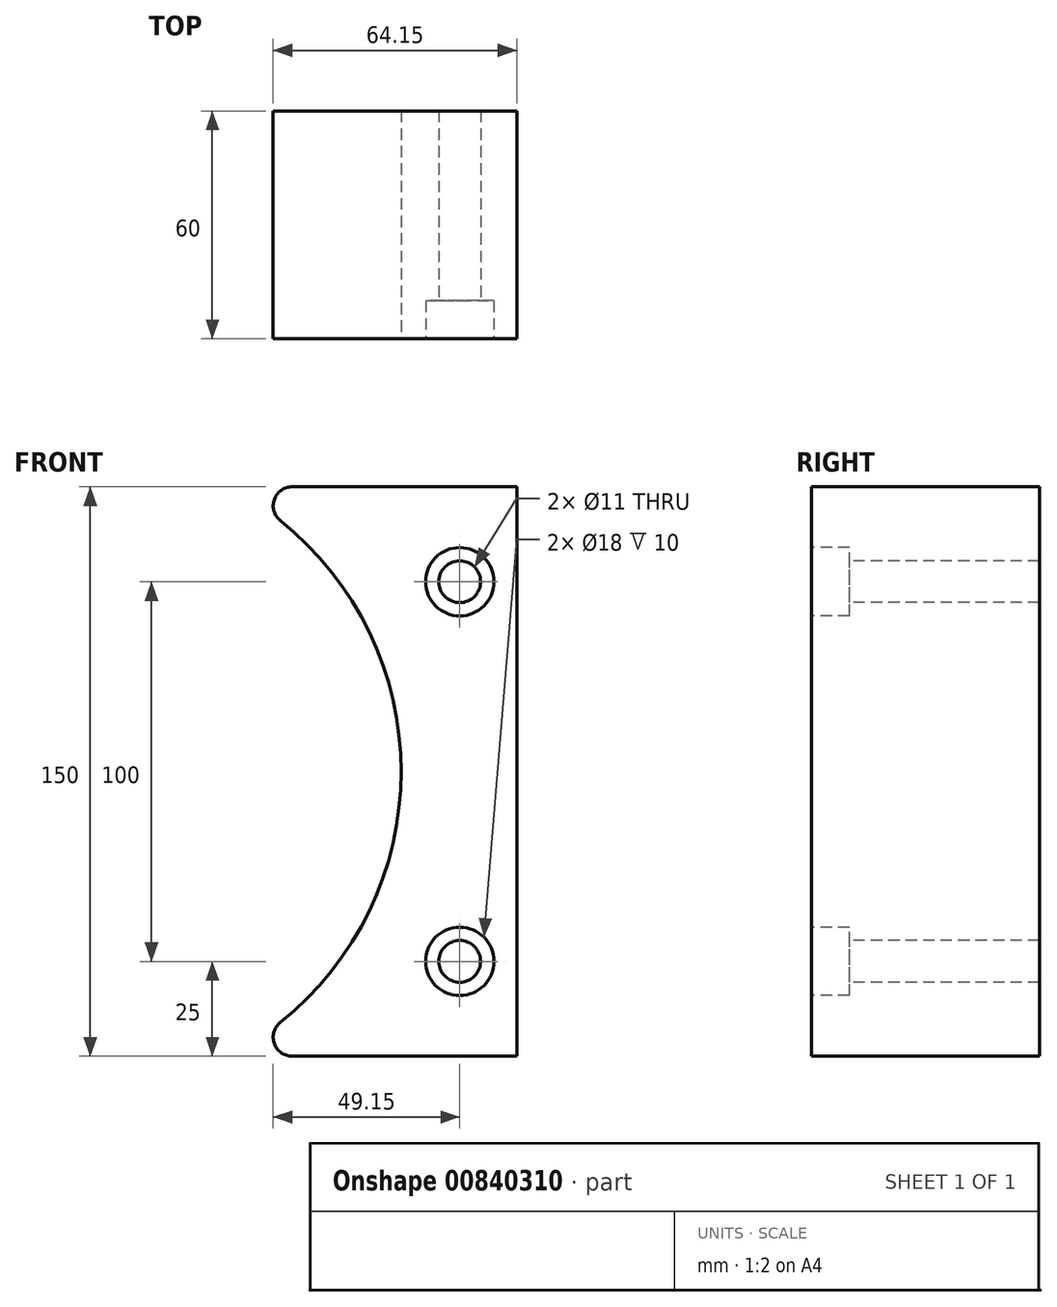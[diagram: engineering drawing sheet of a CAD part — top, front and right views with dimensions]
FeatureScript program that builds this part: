
annotation { "Feature Type Name" : "Feature", "Feature Type Description" : "" }
export const myFeature = defineFeature(function(context is Context, id is Id, definition is map)
    precondition{}
    {
        {
            var Q0;
            Q0=qCreatedBy(makeId("Front.planeOp"),FACE);
            var sketch = newSketch(context, id + "F0", { "sketchPlane" : qUnion([Q0])});
            skLineSegment(sketch, "E0.bottom", {"start": v(-37.5, 75) * mm, "end": v(37.5, 75) * mm});
            skLineSegment(sketch, "E0.top", {"start": v(-37.5, -75) * mm, "end": v(37.5, -75) * mm});
            skLineSegment(sketch, "E0.left", {"start": v(-37.5, 75) * mm, "end": v(-37.5, -75) * mm});
            skLineSegment(sketch, "E0.right", {"start": v(37.5, 75) * mm, "end": v(37.5, -75) * mm});
            skPoint(sketch, "E0.middle", {"position": v(0, 0) * mm});
            skSolve(sketch);
        }
        {
            var Q0;
            Q0 = qSketchRegion(id + "F0", true);
            extrude(context, id + "F1", {"entities" : qUnion([Q0]), "endBound" : BoundingType.SYMMETRIC, "depth" : 60 * mm, "offsetDistance" : 25 * mm});
        }
        {
            var Q0;
            Q0=makeQuery(id+"F1.opExtrude","CAP_FACE",FACE,{"disambiguationData":[OSD([sQuery(id+"F0.wireOp",EDGE,"E0.bottom"),sQuery(id+"F0.wireOp",EDGE,"E0.top"),sQuery(id+"F0.wireOp",EDGE,"E0.left"),sQuery(id+"F0.wireOp",EDGE,"E0.right")])],"isStart":false});
            var sketch = newSketch(context, id + "F2", { "sketchPlane" : qUnion([Q0])});
            skCircle(sketch, "E1", {"center": v(-77.5, 0) * mm, "radius": 84.55 * mm});
            skArc(sketch, "E2", {"start": v(-21.65, 75) * mm, "mid": v(-26.37, 71.65) * mm, "end": v(-24.77, 66.1) * mm});
            skArc(sketch, "E3", {"start": v(-24.77, -66.1) * mm, "mid": v(-26.37, -71.65) * mm, "end": v(-21.65, -75) * mm});
            skSolve(sketch);
        }
        {
            var Q0;
            Q0 = qSketchRegion(id + "F2", true);
            var Q1;
            {var subQ0=sQuery(id+"F2.wireOp",EDGE,"E2");Q1=makeQuery(id+"F2.imprint","IMPRINT",FACE,{"disambiguationData":[TD([[makeQuery(id+"F2.imprint","IMPRINT",EDGE,{"derivedFrom":subQ0}),-1.0]])]});}
            var Q2;
            {var subQ0=sQuery(id+"F2.wireOp",EDGE,"E3");Q2=makeQuery(id+"F2.imprint","IMPRINT",FACE,{"disambiguationData":[TD([[makeQuery(id+"F2.imprint","IMPRINT",EDGE,{"derivedFrom":subQ0}),-1.0]])]});}
            extrude(context, id + "F3", {"entities" : qUnion([Q0, Q1, Q2]), "operationType" : NewBodyOperationType.REMOVE, "endBound" : BoundingType.THROUGH_ALL, "oppositeDirection" : true, "depth" : 25 * mm, "offsetDistance" : 25 * mm});
        }
        {
            var Q0;
            Q0=makeQuery(id+"F1.opExtrude","CAP_FACE",FACE,{"disambiguationData":[OSD([sQuery(id+"F0.wireOp",EDGE,"E0.bottom"),sQuery(id+"F0.wireOp",EDGE,"E0.top"),sQuery(id+"F0.wireOp",EDGE,"E0.left"),sQuery(id+"F0.wireOp",EDGE,"E0.right")])],"isStart":false});
            var sketch = newSketch(context, id + "F4", { "sketchPlane" : qUnion([Q0])});
            skPoint(sketch, "E4", {"position": v(22.5, 50) * mm});
            skPoint(sketch, "E5", {"position": v(22.5, -50) * mm});
            skSolve(sketch);
        }
        {
            var Q0;
            Q0=sQuery(id+"F4.wireOp",VERTEX,"E4");
            var Q1;
            Q1=sQuery(id+"F4.wireOp",VERTEX,"E5");
            var Q2;
            Q2=makeQuery(id+"F1.opExtrude","SWEPT_BODY",BODY,{"disambiguationData":[OSD([sQuery(id+"F0.wireOp",EDGE,"E0.bottom"),sQuery(id+"F0.wireOp",EDGE,"E0.top"),sQuery(id+"F0.wireOp",EDGE,"E0.left"),sQuery(id+"F0.wireOp",EDGE,"E0.right")])]});
            hole(context, id + "F5", {"style" : HoleStyle.C_BORE, "endStyle" : HoleEndStyle.THROUGH, "holeDiameter" : 11 * mm, "cBoreDiameter" : 18 * mm, "cBoreDepth" : 10 * mm, "majorDiameter" : 5 * mm, "isTappedThrough" : true, "tappedDepth" : 12 * mm, "tapClearance" : 3, "startFromSketch" : true, "locations" : qUnion([Q0, Q1]), "scope" : qUnion([Q2])});
        }
    });
